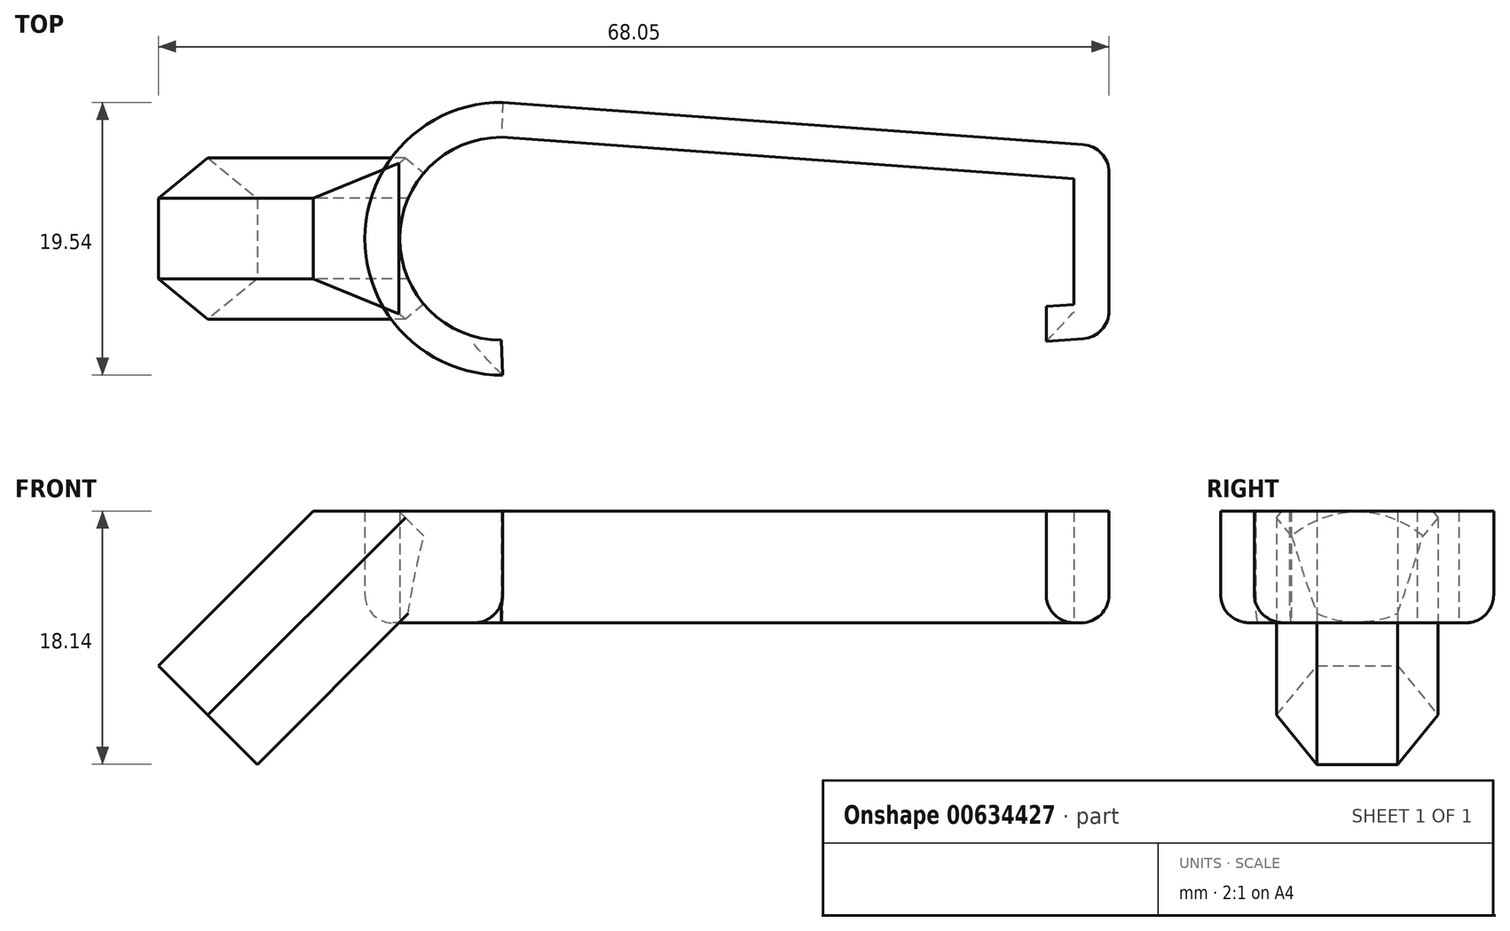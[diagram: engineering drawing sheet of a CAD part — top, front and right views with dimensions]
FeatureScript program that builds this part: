
annotation { "Feature Type Name" : "Feature", "Feature Type Description" : "" }
export const myFeature = defineFeature(function(context is Context, id is Id, definition is map)
    precondition{}
    {
        {
            var Q0;
            Q0=qCreatedBy(makeId("Top.planeOp"),FACE);
            var sketch = newSketch(context, id + "F0", { "sketchPlane" : qUnion([Q0])});
            skLineSegment(sketch, "E0", {"start": v(41, -4.71) * mm, "end": v(41, 4.29) * mm});
            skLineSegment(sketch, "E1", {"start": v(41, 4.29) * mm, "end": v(0, 7.27) * mm});
            skPoint(sketch, "E2", {"position": v(41, -0.21) * mm});
            skLineSegment(sketch, "E3", {"start": v(0, 7.27) * mm, "end": v(41, 7.27) * mm, "construction": true});
            skLineSegment(sketch, "E4", {"start": v(41, 7.27) * mm, "end": v(41, 4.29) * mm, "construction": true});
            skArc(sketch, "E5", {"start": v(0, 7.27) * mm, "mid": v(-7.27, 0) * mm, "end": v(0, -7.27) * mm});
            skLineSegment(sketch, "E6.0", {"start": v(43.5, 6.61) * mm, "end": v(0.1, 9.77) * mm});
            skLineSegment(sketch, "E6.1", {"start": v(43.5, -7.04) * mm, "end": v(43.5, 6.61) * mm});
            skArc(sketch, "E6.3", {"start": v(0.1, 9.77) * mm, "mid": v(-9.77, 0) * mm, "end": v(0.1, -9.77) * mm});
            skLineSegment(sketch, "E7", {"start": v(0, -7.27) * mm, "end": v(0.1, -9.77) * mm});
            skLineSegment(sketch, "E8", {"start": v(41, -4.71) * mm, "end": v(39, -4.86) * mm});
            skLineSegment(sketch, "E9", {"start": v(39, -4.86) * mm, "end": v(39, -7.37) * mm});
            skLineSegment(sketch, "E10", {"start": v(39, -7.37) * mm, "end": v(43.5, -7.04) * mm});
            skLineSegment(sketch, "E11", {"start": v(0, 7.27) * mm, "end": v(0, -7.27) * mm});
            skSolve(sketch);
        }
        {
            var Q0;
            Q0=makeQuery(id+"F0.imprint","IMPRINT",FACE,{"disambiguationData":[TD([[makeQuery(id+"F0.imprint","IMPRINT",EDGE,{"derivedFrom":sQuery(id+"F0.wireOp",EDGE,"E0")}),-1.0]])]});
            extrude(context, id + "F1", {"entities" : qUnion([Q0]), "depth" : 8 * mm, "offsetDistance" : 25 * mm});
        }
        {
            var Q0;
            Q0=makeQuery(id+"F1.opExtrude","SWEPT_EDGE",EDGE,{"disambiguationData":[OSD([sQuery(id+"F0.wireOp",EDGE,"E6.1"),sQuery(id+"F0.wireOp",EDGE,"E6.2")])]});
            var Q1;
            Q1=makeQuery(id+"F1.opExtrude","SWEPT_EDGE",EDGE,{"disambiguationData":[OSD([sQuery(id+"F0.wireOp",EDGE,"E6.0"),sQuery(id+"F0.wireOp",EDGE,"E6.1")])]});
            var Q2;
            Q2=makeQuery(id+"F1.opExtrude","CAP_EDGE",EDGE,{"disambiguationData":[OSD([sQuery(id+"F0.wireOp",EDGE,"E9")])],"isStart":true});
            var Q3;
            Q3=makeQuery(id+"F1.opExtrude","CAP_EDGE",EDGE,{"disambiguationData":[OSD([sQuery(id+"F0.wireOp",EDGE,"E10")])],"isStart":true});
            var Q4;
            Q4=makeQuery(id+"F1.opExtrude","CAP_EDGE",EDGE,{"disambiguationData":[OSD([sQuery(id+"F0.wireOp",EDGE,"E6.1")])],"isStart":true});
            var Q5;
            Q5=makeQuery(id+"F1.opExtrude","CAP_EDGE",EDGE,{"disambiguationData":[OSD([sQuery(id+"F0.wireOp",EDGE,"E6.0")])],"isStart":true});
            var Q6;
            Q6=makeQuery(id+"F1.opExtrude","CAP_EDGE",EDGE,{"disambiguationData":[OSD([sQuery(id+"F0.wireOp",EDGE,"E6.3")])],"isStart":true});
            var Q7;
            Q7=makeQuery(id+"F1.opExtrude","CAP_EDGE",EDGE,{"disambiguationData":[OSD([sQuery(id+"F0.wireOp",EDGE,"E7")])],"isStart":true});
            fillet(context, id + "F2", {"entities" : qUnion([Q0, Q1, Q2, Q3, Q4, Q5, Q6, Q7]), "radius" : 2 * mm, "tangentPropagation" : true, "allowEdgeOverflow" : false});
        }
        {
            var Q0;
            Q0=qCreatedBy(makeId("Top.planeOp"),FACE);
            var sketch = newSketch(context, id + "F3", { "sketchPlane" : qUnion([Q0])});
            skCircle(sketch, "E12.cCircle", {"center": v(-13.33, 0) * mm, "radius": 5 * mm, "construction": true});
            skLineSegment(sketch, "E12.0", {"start": v(-8.33, 2.89) * mm, "end": v(-8.33, -2.89) * mm});
            skLineSegment(sketch, "E12.1", {"start": v(-8.33, -2.89) * mm, "end": v(-13.33, -5.77) * mm});
            skLineSegment(sketch, "E12.2", {"start": v(-13.33, -5.77) * mm, "end": v(-18.33, -2.89) * mm});
            skLineSegment(sketch, "E12.3", {"start": v(-18.33, -2.89) * mm, "end": v(-18.33, 2.89) * mm});
            skLineSegment(sketch, "E12.4", {"start": v(-18.33, 2.89) * mm, "end": v(-13.33, 5.77) * mm});
            skLineSegment(sketch, "E12.5", {"start": v(-13.33, 5.77) * mm, "end": v(-8.33, 2.89) * mm});
            skPoint(sketch, "E12.0.midPoint", {"position": v(-8.33, 0) * mm});
            skSolve(sketch);
        }
        {
            var Q0;
            Q0 = qSketchRegion(id + "F3", true);
            extrude(context, id + "F4", {"entities" : qUnion([Q0]), "depth" : 4 * mm, "offsetDistance" : 25 * mm, "hasSecondDirection" : true, "secondDirectionOppositeDirection" : true, "secondDirectionDepth" : 16 * mm});
        }
        {
            var Q0;
            Q0=makeQuery(id+"F4.opExtrude","SWEPT_BODY",BODY,{"disambiguationData":[OSD([sQuery(id+"F3.wireOp",EDGE,"E12.0"),sQuery(id+"F3.wireOp",EDGE,"E12.1"),sQuery(id+"F3.wireOp",EDGE,"E12.2"),sQuery(id+"F3.wireOp",EDGE,"E12.3"),sQuery(id+"F3.wireOp",EDGE,"E12.4"),sQuery(id+"F3.wireOp",EDGE,"E12.5")])]});
            var Q1;
            Q1=makeQuery(id+"F4.opExtrude","CAP_EDGE",EDGE,{"disambiguationData":[OSD([sQuery(id+"F3.wireOp",EDGE,"E12.0")])],"isStart":false});
            transform(context, id + "F5", {"entities" : qUnion([Q0]), "transformType" : TransformType.ROTATION, "transformAxis" : qUnion([Q1]), "angle" : 45 * degree, "oppositeDirection" : true, "makeCopy" : false});
        }
        {
            var Q0;
            Q0=makeQuery(id+"F4.opExtrude","SWEPT_BODY",BODY,{"disambiguationData":[OSD([sQuery(id+"F3.wireOp",EDGE,"E12.0"),sQuery(id+"F3.wireOp",EDGE,"E12.1"),sQuery(id+"F3.wireOp",EDGE,"E12.2"),sQuery(id+"F3.wireOp",EDGE,"E12.3"),sQuery(id+"F3.wireOp",EDGE,"E12.4"),sQuery(id+"F3.wireOp",EDGE,"E12.5")])]});
            transform(context, id + "F6", {"entities" : qUnion([Q0]), "transformType" : TransformType.TRANSLATION_3D, "dx" : 5 * mm, "dy" : 0 * mm, "dz" : 0 * mm, "makeCopy" : false});
        }
        {
            var Q0;
            Q0=makeQuery(id+"F0.imprint","IMPRINT",FACE,{"disambiguationData":[TD([[makeQuery(id+"F0.imprint","IMPRINT",EDGE,{"derivedFrom":sQuery(id+"F0.wireOp",EDGE,"E5")}),1.0]])]});
            extrude(context, id + "F7", {"entities" : qUnion([Q0]), "operationType" : NewBodyOperationType.REMOVE, "depth" : 25 * mm, "offsetDistance" : 25 * mm});
        }
        {
            var Q0;
            Q0=makeQuery(id+"F1.opExtrude","CAP_FACE",FACE,{"disambiguationData":[OSD([sQuery(id+"F0.wireOp",EDGE,"E0"),sQuery(id+"F0.wireOp",EDGE,"E1"),sQuery(id+"F0.wireOp",EDGE,"E5"),sQuery(id+"F0.wireOp",EDGE,"E6.0"),sQuery(id+"F0.wireOp",EDGE,"E6.1"),sQuery(id+"F0.wireOp",EDGE,"E6.3"),sQuery(id+"F0.wireOp",EDGE,"E7"),sQuery(id+"F0.wireOp",EDGE,"E8"),sQuery(id+"F0.wireOp",EDGE,"E9"),sQuery(id+"F0.wireOp",EDGE,"E10")])],"isStart":false});
            var sketch = newSketch(context, id + "F8", { "sketchPlane" : qUnion([Q0])});
            skLineSegment(sketch, "E13.bottom", {"start": v(-22, -12.15) * mm, "end": v(4.12, -12.15) * mm});
            skLineSegment(sketch, "E13.top", {"start": v(-22, 16.16) * mm, "end": v(4.12, 16.16) * mm});
            skLineSegment(sketch, "E13.left", {"start": v(-22, -12.15) * mm, "end": v(-22, 16.16) * mm});
            skLineSegment(sketch, "E13.right", {"start": v(4.12, -12.15) * mm, "end": v(4.12, 16.16) * mm});
            skSolve(sketch);
        }
        {
            var Q0;
            Q0 = qSketchRegion(id + "F8", true);
            extrude(context, id + "F9", {"entities" : qUnion([Q0]), "operationType" : NewBodyOperationType.REMOVE, "depth" : 25 * mm, "offsetDistance" : 25 * mm});
        }
    });
